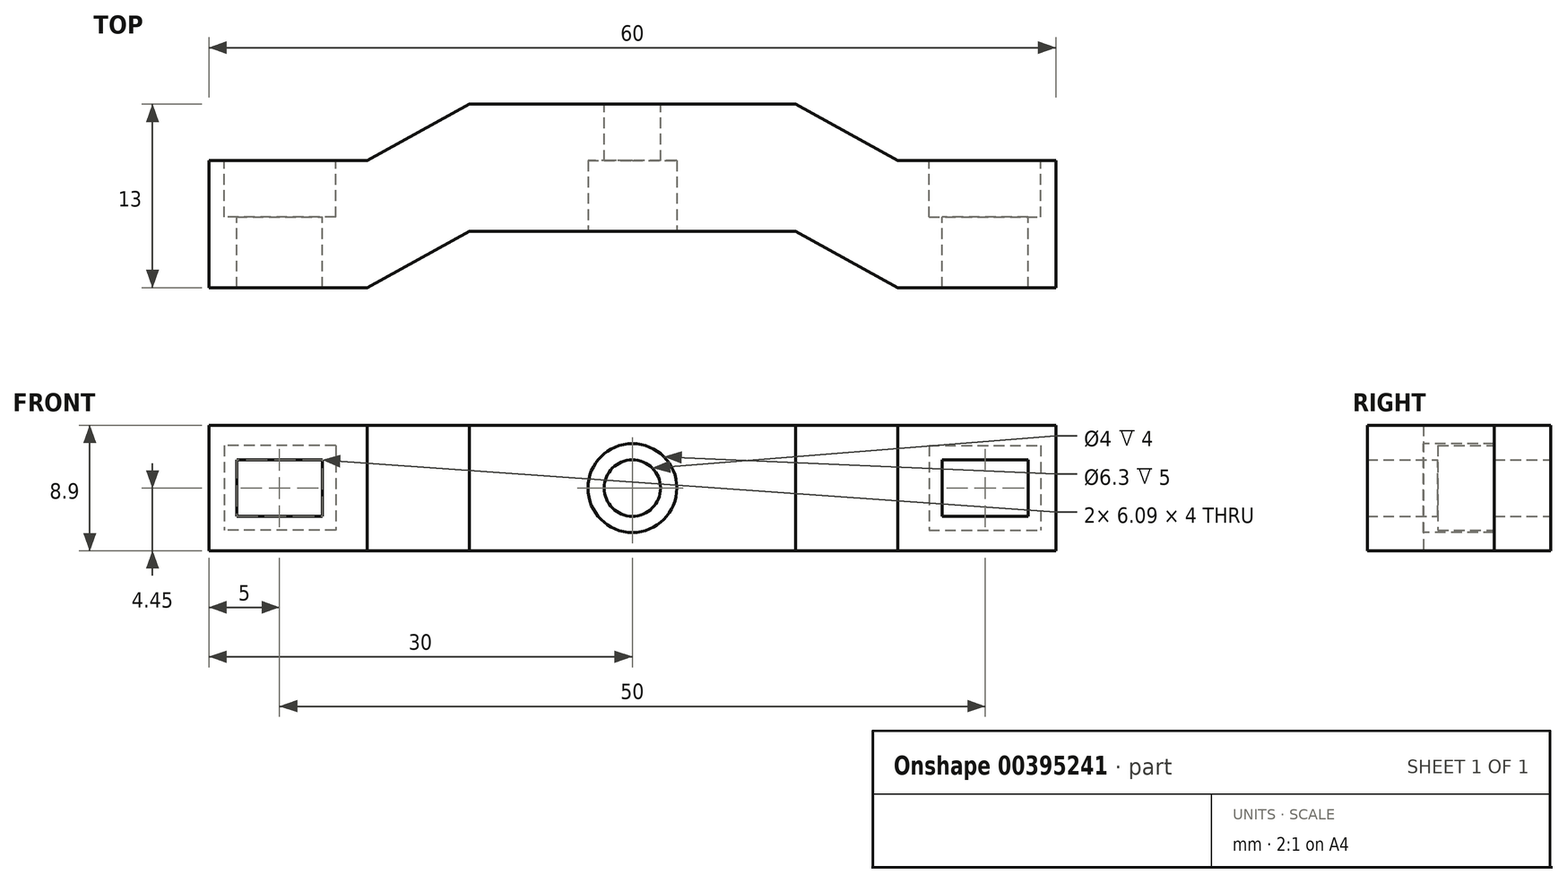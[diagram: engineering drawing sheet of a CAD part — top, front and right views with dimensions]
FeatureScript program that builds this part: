
annotation { "Feature Type Name" : "Feature", "Feature Type Description" : "" }
export const myFeature = defineFeature(function(context is Context, id is Id, definition is map)
    precondition{}
    {
        {
            var Q0;
            Q0=qCreatedBy(makeId("Top.planeOp"),FACE);
            var sketch = newSketch(context, id + "F0", { "sketchPlane" : qUnion([Q0])});
            skLineSegment(sketch, "E0", {"start": v(-30, 0) * mm, "end": v(-18.79, 0) * mm});
            skLineSegment(sketch, "E1", {"start": v(-18.79, 0) * mm, "end": v(-11.56, 4) * mm});
            skLineSegment(sketch, "E2", {"start": v(-30, 0) * mm, "end": v(-30, 9) * mm});
            skLineSegment(sketch, "E3", {"start": v(-30, 9) * mm, "end": v(-18.79, 9) * mm});
            skLineSegment(sketch, "E4", {"start": v(-18.79, 9) * mm, "end": v(-11.56, 13) * mm});
            skLineSegment(sketch, "E5", {"start": v(-11.56, 13) * mm, "end": v(0, 13) * mm});
            skLineSegment(sketch, "E6", {"start": v(-11.56, 4) * mm, "end": v(0, 4) * mm});
            skLineSegment(sketch, "E7.MirrorCS", {"start": v(11.56, 13) * mm, "end": v(0, 13) * mm});
            skLineSegment(sketch, "E8.MirrorCS", {"start": v(11.56, 4) * mm, "end": v(0, 4) * mm});
            skLineSegment(sketch, "E9.MirrorCS", {"start": v(18.79, 0) * mm, "end": v(11.56, 4) * mm});
            skLineSegment(sketch, "E10.MirrorCS", {"start": v(18.79, 9) * mm, "end": v(11.56, 13) * mm});
            skLineSegment(sketch, "E11.MirrorCS", {"start": v(30, 9) * mm, "end": v(18.79, 9) * mm});
            skLineSegment(sketch, "E12.MirrorCS", {"start": v(30, 0) * mm, "end": v(30, 9) * mm});
            skLineSegment(sketch, "E13.MirrorCS", {"start": v(30, 0) * mm, "end": v(18.79, 0) * mm});
            skSolve(sketch);
        }
        {
            var Q0;
            Q0=makeQuery(id+"F0.imprint","IMPRINT",FACE,{"disambiguationData":[TD([[makeQuery(id+"F0.imprint","IMPRINT",EDGE,{"derivedFrom":sQuery(id+"F0.wireOp",EDGE,"E0")}),1.0]])]});
            extrude(context, id + "F1", {"entities" : qUnion([Q0]), "endBound" : BoundingType.SYMMETRIC, "depth" : 8.9 * mm});
        }
        {
            var Q0;
            Q0=makeQuery(id+"F1.opExtrude","SWEPT_FACE",FACE,{"disambiguationData":[OSD([sQuery(id+"F0.wireOp",EDGE,"E5"),sQuery(id+"F0.wireOp",EDGE,"E7.MirrorCS")])]});
            var sketch = newSketch(context, id + "F2", { "sketchPlane" : qUnion([Q0])});
            skCircle(sketch, "E14", {"center": v(0, 0) * mm, "radius": 2 * mm});
            skLineSegment(sketch, "E15.bottom", {"start": v(-21.96, 2) * mm, "end": v(-28.04, 2) * mm});
            skLineSegment(sketch, "E15.top", {"start": v(-21.96, -2) * mm, "end": v(-28.04, -2) * mm});
            skLineSegment(sketch, "E15.left", {"start": v(-21.96, 2) * mm, "end": v(-21.96, -2) * mm});
            skLineSegment(sketch, "E15.right", {"start": v(-28.04, 2) * mm, "end": v(-28.04, -2) * mm});
            skPoint(sketch, "E15.middle", {"position": v(-25, 0) * mm});
            skLineSegment(sketch, "E16.MirrorCS", {"start": v(21.96, 2) * mm, "end": v(28.04, 2) * mm});
            skLineSegment(sketch, "E17.MirrorCS", {"start": v(21.96, 2) * mm, "end": v(21.96, -2) * mm});
            skLineSegment(sketch, "E18.MirrorCS", {"start": v(21.96, -2) * mm, "end": v(28.04, -2) * mm});
            skLineSegment(sketch, "E19.MirrorCS", {"start": v(28.04, 2) * mm, "end": v(28.04, -2) * mm});
            skSolve(sketch);
        }
        {
            var Q0;
            Q0 = qSketchRegion(id + "F2", true);
            extrude(context, id + "F3", {"entities" : qUnion([Q0]), "operationType" : NewBodyOperationType.REMOVE, "oppositeDirection" : true, "depth" : 25 * mm});
        }
        {
            var Q0;
            Q0=makeQuery(id+"F1.opExtrude","SWEPT_FACE",FACE,{"disambiguationData":[OSD([sQuery(id+"F0.wireOp",EDGE,"E6"),sQuery(id+"F0.wireOp",EDGE,"E8.MirrorCS")])]});
            var sketch = newSketch(context, id + "F4", { "sketchPlane" : qUnion([Q0])});
            skCircle(sketch, "E20", {"center": v(0, 0) * mm, "radius": 3.15 * mm});
            skSolve(sketch);
        }
        {
            var Q0;
            Q0 = qSketchRegion(id + "F4", true);
            extrude(context, id + "F5", {"entities" : qUnion([Q0]), "operationType" : NewBodyOperationType.REMOVE, "oppositeDirection" : true, "depth" : 5 * mm});
        }
        {
            var Q0;
            Q0=makeQuery(id+"F1.opExtrude","SWEPT_FACE",FACE,{"disambiguationData":[OSD([sQuery(id+"F0.wireOp",EDGE,"E3")])]});
            var sketch = newSketch(context, id + "F6", { "sketchPlane" : qUnion([Q0])});
            skLineSegment(sketch, "E21.bottom", {"start": v(-21.01, 3) * mm, "end": v(-28.93, 3) * mm});
            skLineSegment(sketch, "E21.top", {"start": v(-21.01, -3) * mm, "end": v(-28.93, -3) * mm});
            skLineSegment(sketch, "E21.left", {"start": v(-21.01, 3) * mm, "end": v(-21.01, -3) * mm});
            skLineSegment(sketch, "E21.right", {"start": v(-28.93, 3) * mm, "end": v(-28.93, -3) * mm});
            skPoint(sketch, "E21.middle", {"position": v(-24.97, 0) * mm});
            skLineSegment(sketch, "E22.MirrorCS", {"start": v(21.01, 3) * mm, "end": v(28.93, 3) * mm});
            skLineSegment(sketch, "E23.MirrorCS", {"start": v(28.93, 3) * mm, "end": v(28.93, -3) * mm});
            skLineSegment(sketch, "E24.MirrorCS", {"start": v(21.01, -3) * mm, "end": v(28.93, -3) * mm});
            skLineSegment(sketch, "E25.MirrorCS", {"start": v(21.01, 3) * mm, "end": v(21.01, -3) * mm});
            skSolve(sketch);
        }
        {
            var Q0;
            Q0 = qSketchRegion(id + "F6", true);
            extrude(context, id + "F7", {"entities" : qUnion([Q0]), "operationType" : NewBodyOperationType.REMOVE, "oppositeDirection" : true, "depth" : 4 * mm});
        }
    });
